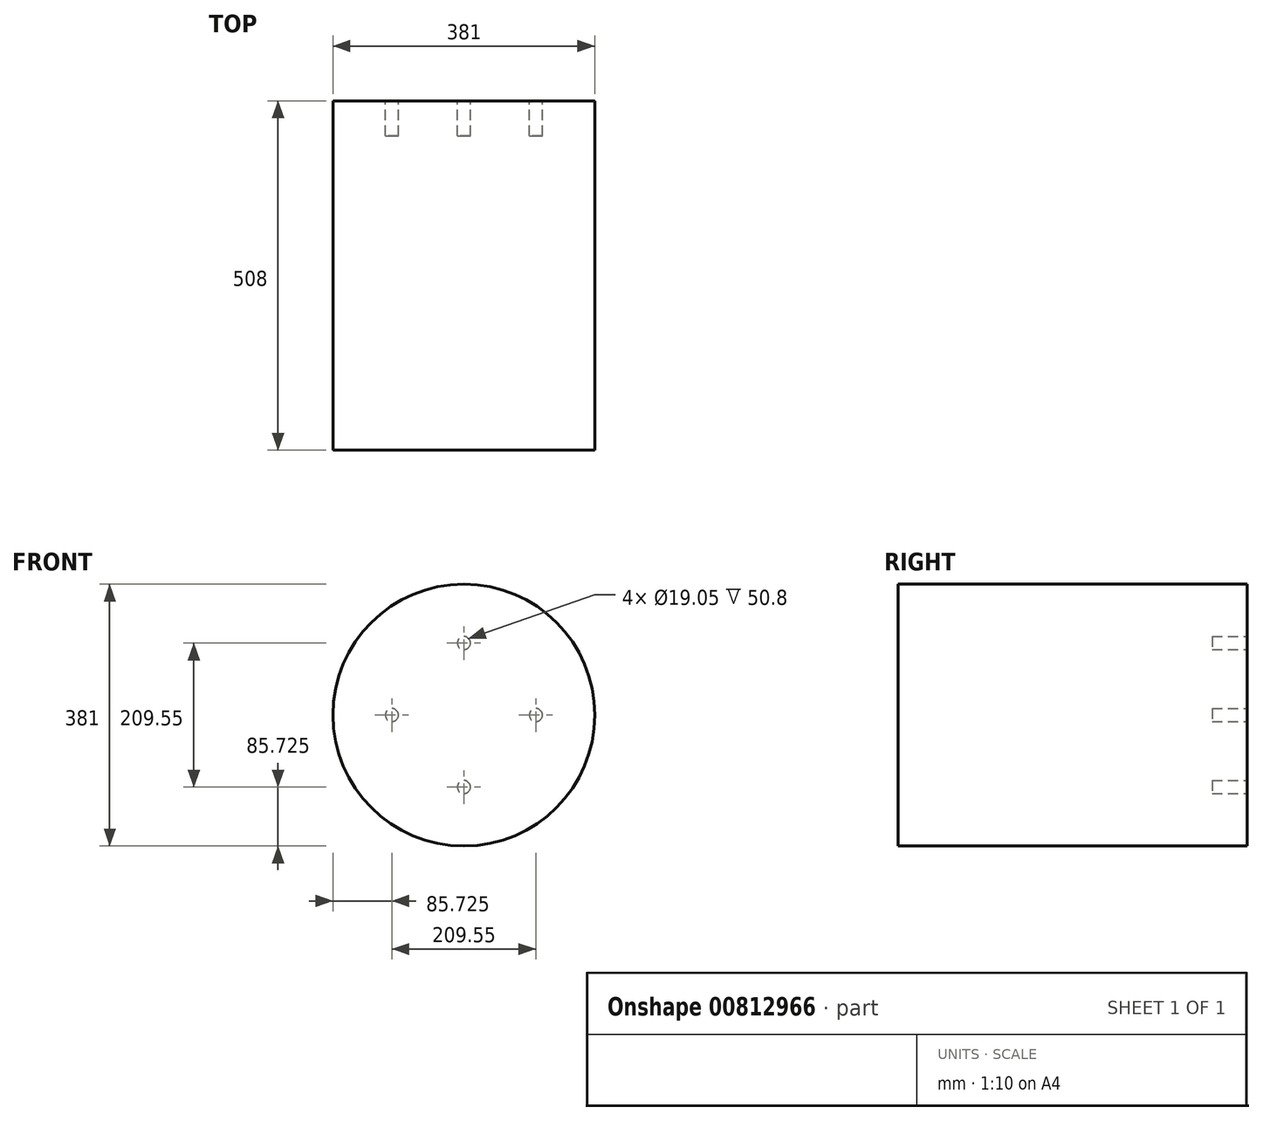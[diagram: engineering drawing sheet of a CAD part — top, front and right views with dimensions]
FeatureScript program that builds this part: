
annotation { "Feature Type Name" : "Feature", "Feature Type Description" : "" }
export const myFeature = defineFeature(function(context is Context, id is Id, definition is map)
    precondition{}
    {
        {
            var Q0;
            Q0=qCreatedBy(makeId("Front.planeOp"),FACE);
            var sketch = newSketch(context, id + "F0", { "sketchPlane" : qUnion([Q0])});
            skCircle(sketch, "E0", {"center": v(0, 0) * mm, "radius": 190.5 * mm});
            skSolve(sketch);
        }
        {
            var Q0;
            Q0 = qSketchRegion(id + "F0", true);
            extrude(context, id + "F1", {"entities" : qUnion([Q0]), "depth" : 508 * mm, "offsetDistance" : 25.4 * mm});
        }
        {
            var Q0;
            Q0=makeQuery(id+"F1.opExtrude","CAP_FACE",FACE,{"disambiguationData":[OSD([sQuery(id+"F0.wireOp",EDGE,"E0")])],"isStart":true});
            var sketch = newSketch(context, id + "F2", { "sketchPlane" : qUnion([Q0])});
            skCircle(sketch, "E1", {"center": v(0, 0) * mm, "radius": 104.78 * mm, "construction": true});
            skLineSegment(sketch, "E2", {"start": v(0, 403.12) * mm, "end": v(0, -442.27) * mm, "construction": true});
            skLineSegment(sketch, "E3", {"start": v(-377.33, 0) * mm, "end": v(519.4, 0) * mm, "construction": true});
            skCircle(sketch, "E4", {"center": v(0, 104.78) * mm, "radius": 9.53 * mm});
            skCircle(sketch, "E5", {"center": v(104.78, 0) * mm, "radius": 9.52 * mm});
            skCircle(sketch, "E6", {"center": v(0, -104.78) * mm, "radius": 9.52 * mm});
            skCircle(sketch, "E7", {"center": v(-104.78, 0) * mm, "radius": 9.52 * mm});
            skSolve(sketch);
        }
        {
            var Q0;
            Q0 = qSketchRegion(id + "F2", true);
            extrude(context, id + "F3", {"entities" : qUnion([Q0]), "operationType" : NewBodyOperationType.REMOVE, "oppositeDirection" : true, "depth" : 50.8 * mm, "offsetDistance" : 25.4 * mm});
        }
    });
